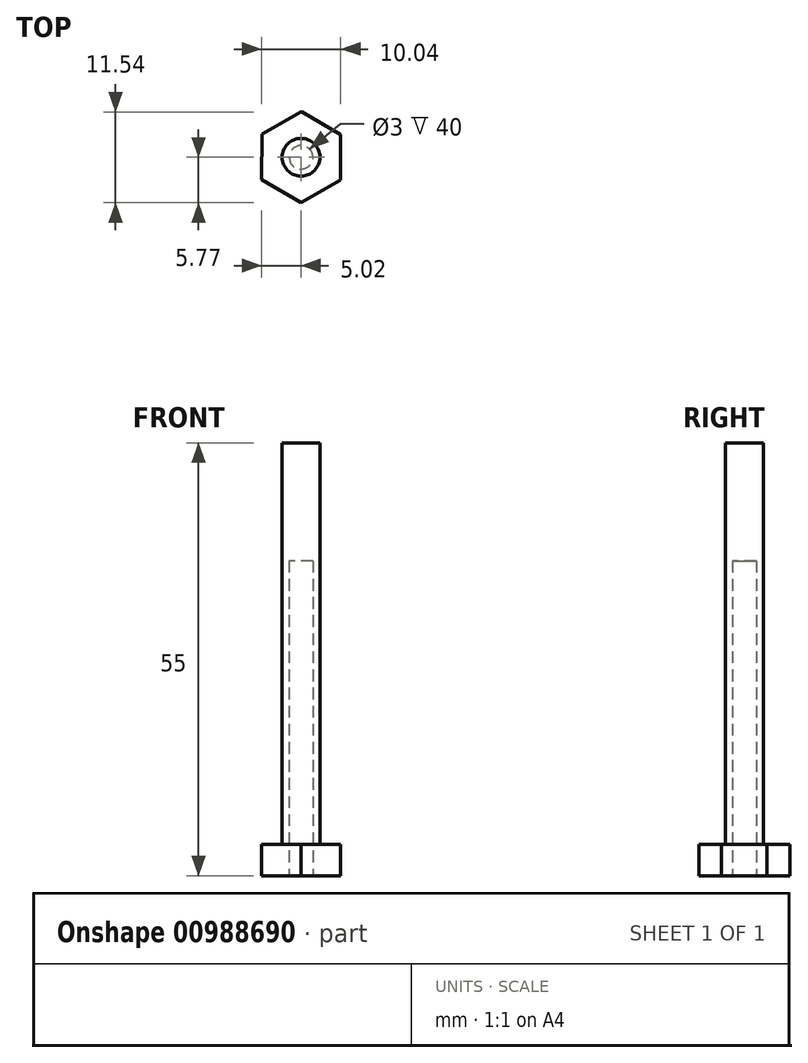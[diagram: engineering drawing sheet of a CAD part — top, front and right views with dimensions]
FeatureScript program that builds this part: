
annotation { "Feature Type Name" : "Feature", "Feature Type Description" : "" }
export const myFeature = defineFeature(function(context is Context, id is Id, definition is map)
    precondition{}
    {
        {
            var Q0;
            Q0=qCreatedBy(makeId("Top.planeOp"),FACE);
            var sketch = newSketch(context, id + "F0", { "sketchPlane" : qUnion([Q0])});
            skCircle(sketch, "E0.cCircle", {"center": v(0, 0) * mm, "radius": 5.77 * mm, "construction": true});
            skLineSegment(sketch, "E0.0", {"start": v(4.98, -2.91) * mm, "end": v(-0.03, -5.77) * mm});
            skLineSegment(sketch, "E0.1", {"start": v(-0.03, -5.77) * mm, "end": v(-5.02, -2.86) * mm});
            skLineSegment(sketch, "E0.2", {"start": v(-5.02, -2.86) * mm, "end": v(-4.98, 2.91) * mm});
            skLineSegment(sketch, "E0.3", {"start": v(-4.98, 2.91) * mm, "end": v(0.03, 5.77) * mm});
            skLineSegment(sketch, "E0.4", {"start": v(0.03, 5.77) * mm, "end": v(5.02, 2.86) * mm});
            skLineSegment(sketch, "E0.5", {"start": v(5.02, 2.86) * mm, "end": v(4.98, -2.91) * mm});
            skSolve(sketch);
        }
        {
            var Q0;
            Q0 = qSketchRegion(id + "F0", true);
            extrude(context, id + "F1", {"entities" : qUnion([Q0]), "depth" : 4 * mm, "offsetDistance" : 25 * mm});
        }
        {
            var Q0;
            Q0=makeQuery(id+"F0.imprint","IMPRINT",FACE,{"disambiguationData":[TD([[makeQuery(id+"F0.imprint","IMPRINT",EDGE,{"derivedFrom":sQuery(id+"F0.wireOp",EDGE,"E0.0")}),-1.0]])]});
            var sketch = newSketch(context, id + "F2", { "sketchPlane" : qUnion([Q0])});
            skCircle(sketch, "E1", {"center": v(0, 0) * mm, "radius": 2.4 * mm});
            skSolve(sketch);
        }
        {
            var Q0;
            Q0 = qSketchRegion(id + "F2", true);
            extrude(context, id + "F3", {"entities" : qUnion([Q0]), "operationType" : NewBodyOperationType.ADD, "depth" : 55 * mm, "offsetDistance" : 25 * mm});
        }
        {
            var Q0;
            Q0=qCreatedBy(makeId("Top.planeOp"),FACE);
            var sketch = newSketch(context, id + "F4", { "sketchPlane" : qUnion([Q0])});
            skCircle(sketch, "E2", {"center": v(0, 0) * mm, "radius": 1.5 * mm});
            skSolve(sketch);
        }
        {
            var Q0;
            Q0 = qSketchRegion(id + "F4", true);
            extrude(context, id + "F5", {"entities" : qUnion([Q0]), "operationType" : NewBodyOperationType.REMOVE, "depth" : 40 * mm, "offsetDistance" : 25 * mm});
        }
    });
